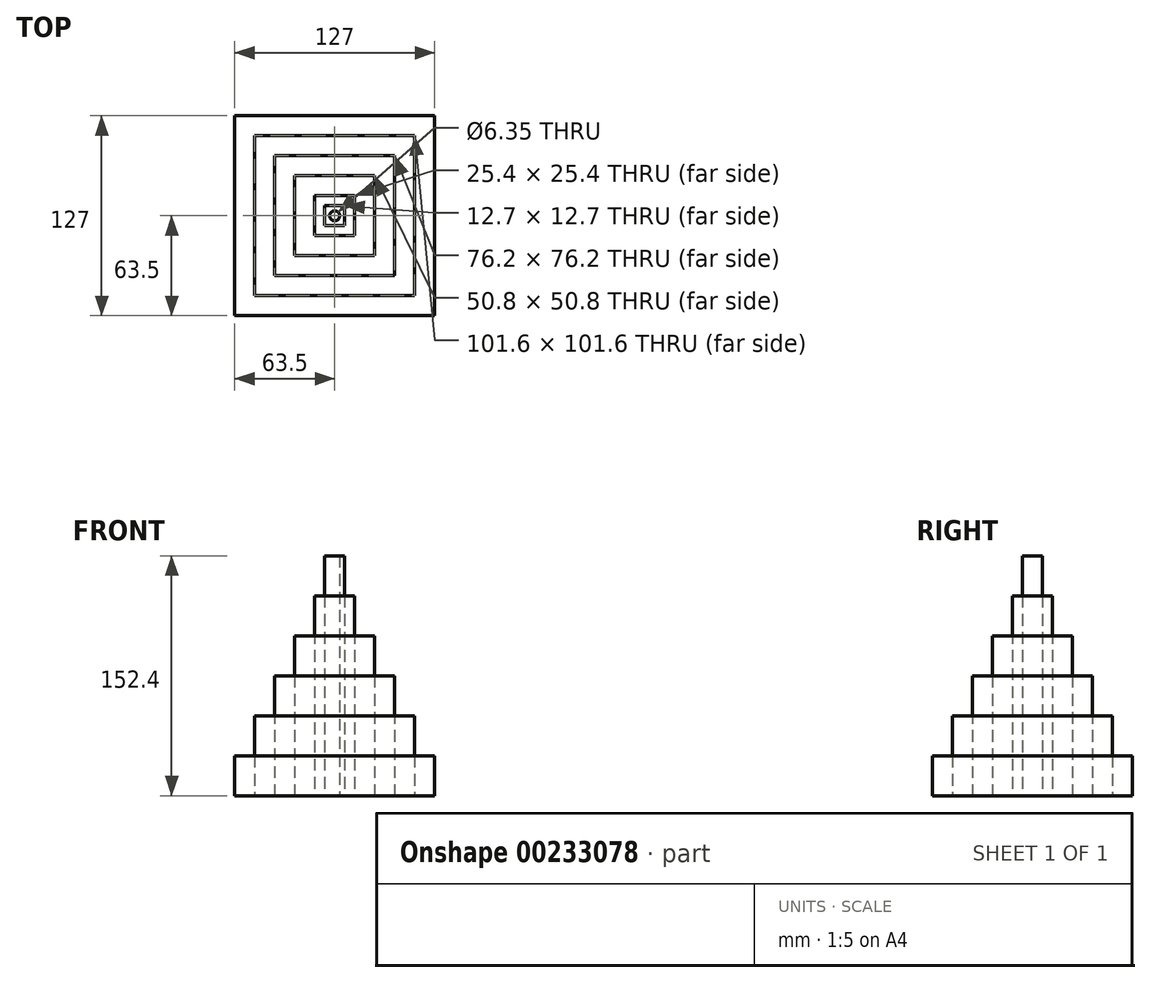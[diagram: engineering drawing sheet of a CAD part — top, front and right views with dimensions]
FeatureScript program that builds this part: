
annotation { "Feature Type Name" : "Feature", "Feature Type Description" : "" }
export const myFeature = defineFeature(function(context is Context, id is Id, definition is map)
    precondition{}
    {
        {
            var Q0;
            Q0=qCreatedBy(makeId("Top.planeOp"),FACE);
            var sketch = newSketch(context, id + "F0", { "sketchPlane" : qUnion([Q0])});
            skLineSegment(sketch, "E0.bottom", {"start": v(63.5, 63.5) * mm, "end": v(-63.5, 63.5) * mm});
            skLineSegment(sketch, "E0.top", {"start": v(63.5, -63.5) * mm, "end": v(-63.5, -63.5) * mm});
            skLineSegment(sketch, "E0.left", {"start": v(63.5, 63.5) * mm, "end": v(63.5, -63.5) * mm});
            skLineSegment(sketch, "E0.right", {"start": v(-63.5, 63.5) * mm, "end": v(-63.5, -63.5) * mm});
            skPoint(sketch, "E0.middle", {"position": v(0, 0) * mm});
            skLineSegment(sketch, "E1.bottom", {"start": v(50.8, 50.8) * mm, "end": v(-50.8, 50.8) * mm});
            skLineSegment(sketch, "E1.top", {"start": v(50.8, -50.8) * mm, "end": v(-50.8, -50.8) * mm});
            skLineSegment(sketch, "E1.left", {"start": v(50.8, 50.8) * mm, "end": v(50.8, -50.8) * mm});
            skLineSegment(sketch, "E1.right", {"start": v(-50.8, 50.8) * mm, "end": v(-50.8, -50.8) * mm});
            skLineSegment(sketch, "E2.bottom", {"start": v(38.1, 38.1) * mm, "end": v(-38.1, 38.1) * mm});
            skLineSegment(sketch, "E2.top", {"start": v(38.1, -38.1) * mm, "end": v(-38.1, -38.1) * mm});
            skLineSegment(sketch, "E2.left", {"start": v(38.1, 38.1) * mm, "end": v(38.1, -38.1) * mm});
            skLineSegment(sketch, "E2.right", {"start": v(-38.1, 38.1) * mm, "end": v(-38.1, -38.1) * mm});
            skPoint(sketch, "E3.middle", {"position": v(0, -2.02) * mm});
            skLineSegment(sketch, "E4.bottom", {"start": v(25.4, 25.4) * mm, "end": v(-25.4, 25.4) * mm});
            skLineSegment(sketch, "E4.top", {"start": v(25.4, -25.4) * mm, "end": v(-25.4, -25.4) * mm});
            skLineSegment(sketch, "E4.left", {"start": v(25.4, 25.4) * mm, "end": v(25.4, -25.4) * mm});
            skLineSegment(sketch, "E4.right", {"start": v(-25.4, 25.4) * mm, "end": v(-25.4, -25.4) * mm});
            skLineSegment(sketch, "E5.bottom", {"start": v(12.7, 12.7) * mm, "end": v(-12.7, 12.7) * mm});
            skLineSegment(sketch, "E5.top", {"start": v(12.7, -12.7) * mm, "end": v(-12.7, -12.7) * mm});
            skLineSegment(sketch, "E5.left", {"start": v(12.7, 12.7) * mm, "end": v(12.7, -12.7) * mm});
            skLineSegment(sketch, "E5.right", {"start": v(-12.7, 12.7) * mm, "end": v(-12.7, -12.7) * mm});
            skLineSegment(sketch, "E6.bottom", {"start": v(6.35, -6.35) * mm, "end": v(-6.35, -6.35) * mm});
            skLineSegment(sketch, "E6.top", {"start": v(6.35, 6.35) * mm, "end": v(-6.35, 6.35) * mm});
            skLineSegment(sketch, "E6.left", {"start": v(6.35, -6.35) * mm, "end": v(6.35, 6.35) * mm});
            skLineSegment(sketch, "E6.right", {"start": v(-6.35, -6.35) * mm, "end": v(-6.35, 6.35) * mm});
            skCircle(sketch, "E7", {"center": v(0, 0) * mm, "radius": 3.18 * mm});
            skSolve(sketch);
        }
        {
            var Q0;
            Q0 = qSketchRegion(id + "F0", true);
            extrude(context, id + "F1", {"entities" : qUnion([Q0]), "depth" : 25.4 * mm});
        }
        {
            var Q0;
            Q0=makeQuery(id+"F0.imprint","IMPRINT",FACE,{"disambiguationData":[TD([[makeQuery(id+"F0.imprint","IMPRINT",EDGE,{"derivedFrom":sQuery(id+"F0.wireOp",EDGE,"E1.bottom")}),1.0]])]});
            extrude(context, id + "F2", {"entities" : qUnion([Q0]), "depth" : 50.8 * mm});
        }
        {
            var Q0;
            Q0=makeQuery(id+"F0.imprint","IMPRINT",FACE,{"disambiguationData":[TD([[makeQuery(id+"F0.imprint","IMPRINT",EDGE,{"derivedFrom":sQuery(id+"F0.wireOp",EDGE,"E2.bottom")}),1.0]])]});
            extrude(context, id + "F3", {"entities" : qUnion([Q0]), "depth" : 76.2 * mm});
        }
        {
            var Q0;
            Q0=makeQuery(id+"F0.imprint","IMPRINT",FACE,{"disambiguationData":[TD([[makeQuery(id+"F0.imprint","IMPRINT",EDGE,{"derivedFrom":sQuery(id+"F0.wireOp",EDGE,"E4.bottom")}),1.0]])]});
            extrude(context, id + "F4", {"entities" : qUnion([Q0]), "depth" : 101.6 * mm});
        }
        {
            var Q0;
            Q0=makeQuery(id+"F0.imprint","IMPRINT",FACE,{"disambiguationData":[TD([[makeQuery(id+"F0.imprint","IMPRINT",EDGE,{"derivedFrom":sQuery(id+"F0.wireOp",EDGE,"E5.bottom")}),1.0]])]});
            extrude(context, id + "F5", {"entities" : qUnion([Q0]), "depth" : 127 * mm});
        }
        {
            var Q0;
            Q0=makeQuery(id+"F0.imprint","IMPRINT",FACE,{"disambiguationData":[TD([[makeQuery(id+"F0.imprint","IMPRINT",EDGE,{"derivedFrom":sQuery(id+"F0.wireOp",EDGE,"E6.bottom")}),-1.0]])]});
            extrude(context, id + "F6", {"entities" : qUnion([Q0]), "depth" : 152.4 * mm});
        }
        {
            var Q0;
            Q0=sQuery(id+"F0.wireOp",EDGE,"E7");
            extrude(context, id + "F7", {"bodyType" : ToolBodyType.SURFACE, "surfaceEntities" : qUnion([Q0]), "depth" : 25.4 * mm});
        }
    });
